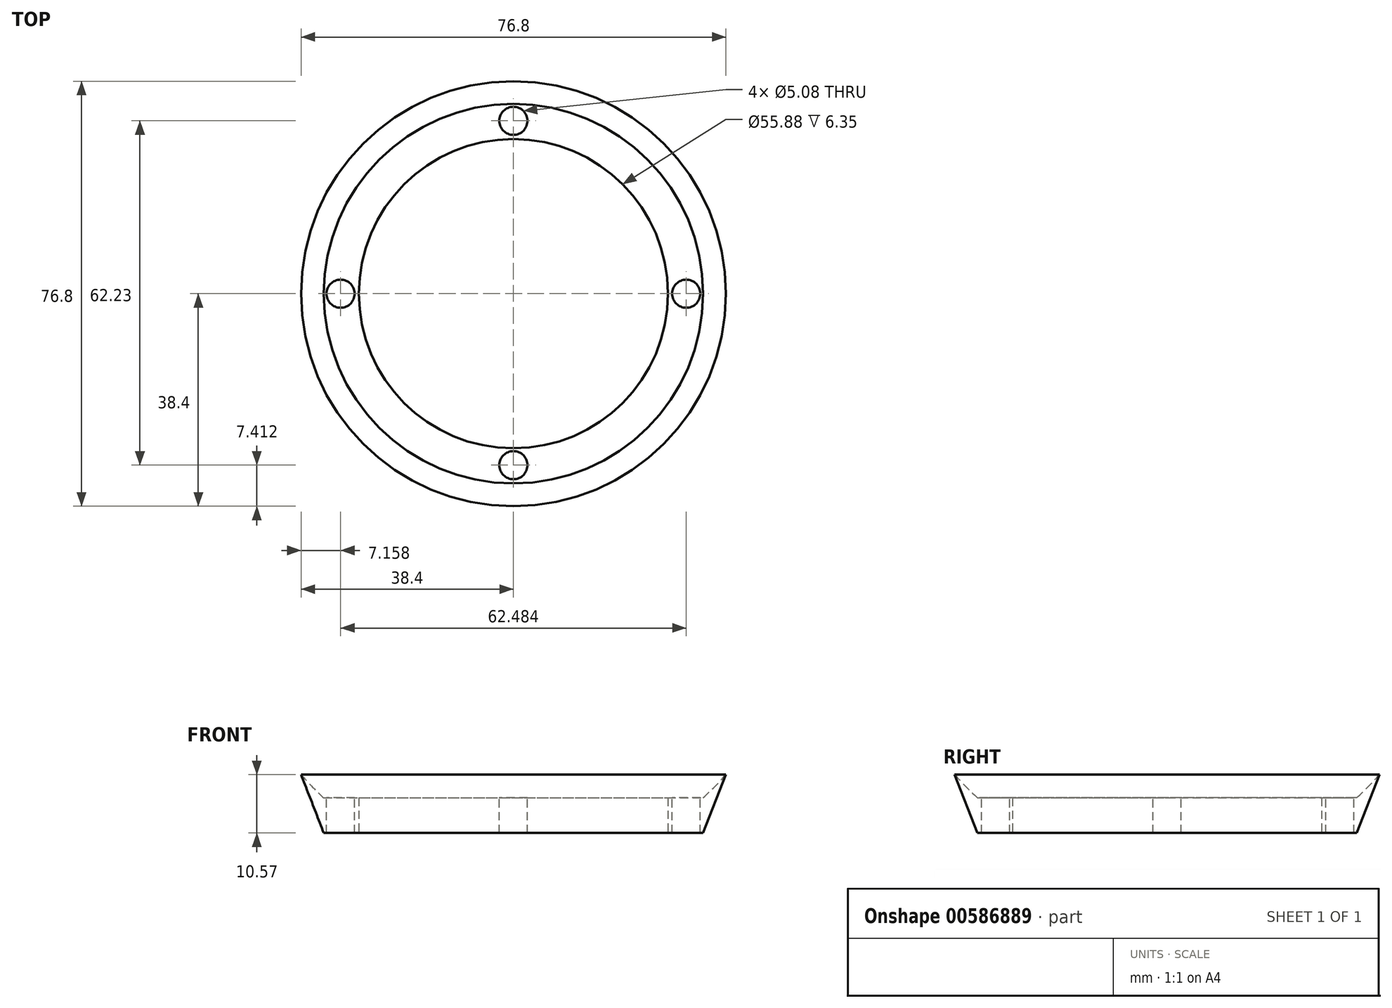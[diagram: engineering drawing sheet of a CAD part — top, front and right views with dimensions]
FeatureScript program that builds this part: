
annotation { "Feature Type Name" : "Feature", "Feature Type Description" : "" }
export const myFeature = defineFeature(function(context is Context, id is Id, definition is map)
    precondition{}
    {
        {
            var Q0;
            Q0=qCreatedBy(makeId("Front.planeOp"),FACE);
            var sketch = newSketch(context, id + "F0", { "sketchPlane" : qUnion([Q0])});
            skArc(sketch, "E0", {"start": v(0, 50.8) * mm, "mid": v(47.35, 18.4) * mm, "end": v(34.3, -37.48) * mm});
            skArc(sketch, "E1.0", {"start": v(0, 48.26) * mm, "mid": v(44.99, 17.47) * mm, "end": v(32.58, -35.6) * mm});
            skLineSegment(sketch, "E2", {"start": v(32.58, -35.6) * mm, "end": v(34.3, -37.48) * mm});
            skLineSegment(sketch, "E3", {"start": v(0, 48.26) * mm, "end": v(0, 50.8) * mm});
            skLineSegment(sketch, "E4.bottom", {"start": v(34.3, -37.48) * mm, "end": v(27.94, -37.48) * mm});
            skLineSegment(sketch, "E4.top", {"start": v(34.3, -43.83) * mm, "end": v(27.94, -43.83) * mm});
            skLineSegment(sketch, "E4.left", {"start": v(34.3, -37.48) * mm, "end": v(34.3, -43.83) * mm});
            skLineSegment(sketch, "E4.right", {"start": v(27.94, -37.48) * mm, "end": v(27.94, -43.83) * mm});
            skLineSegment(sketch, "E5", {"start": v(32.58, -35.6) * mm, "end": v(27.94, -37.48) * mm});
            skLineSegment(sketch, "E6", {"start": v(34.3, -43.83) * mm, "end": v(38.4, -33.26) * mm});
            skSolve(sketch);
        }
        {
            var Q0;
            Q0=makeQuery(id+"F0.imprint","IMPRINT",FACE,{"disambiguationData":[TD([[makeQuery(id+"F0.imprint","IMPRINT",EDGE,{"derivedFrom":sQuery(id+"F0.wireOp",EDGE,"E0")}),-1.0]])]});
            var Q1;
            Q1=makeQuery(id+"F0.imprint","IMPRINT",FACE,{"disambiguationData":[TD([[makeQuery(id+"F0.imprint","IMPRINT",EDGE,{"derivedFrom":sQuery(id+"F0.wireOp",EDGE,"E4.bottom")}),1.0]])]});
            var Q2;
            {var subQ0=sQuery(id+"F0.wireOp",EDGE,"E4.left");Q2=makeQuery(id+"F0.imprint","IMPRINT",FACE,{"disambiguationData":[TD([[makeQuery(id+"F0.imprint","IMPRINT",EDGE,{"derivedFrom":subQ0}),1.0]])]});}
            var Q3;
            Q3=sQuery(id+"F0.wireOp",EDGE,"E3");
            revolve(context, id + "F1", {"entities" : qUnion([Q0, Q1, Q2]), "axis" : qUnion([Q3]), "revolveType" : RevolveType.FULL});
        }
        {
            var Q0;
            Q0=sQuery(id+"F0.wireOp",VERTEX,"E1.0.center");
            var Q1;
            Q1=makeQuery(id+"F1.opRevolve","SWEPT_BODY",BODY,{"disambiguationData":[OSD([sQuery(id+"F0.wireOp",EDGE,"E0"),sQuery(id+"F0.wireOp",EDGE,"E1.0"),sQuery(id+"F0.wireOp",EDGE,"E2"),sQuery(id+"F0.wireOp",EDGE,"E3")])]});
            hole(context, id + "F2", {"style" : HoleStyle.SIMPLE, "endStyle" : HoleEndStyle.THROUGH, "oppositeDirection" : true, "holeDiameter" : 25.4 * mm, "majorDiameter" : 6.35 * mm, "isTappedThrough" : true, "tappedDepth" : 12.7 * mm, "tapClearance" : 3, "startFromSketch" : true, "locations" : qUnion([Q0]), "scope" : qUnion([Q1])});
        }
        {
            var Q0;
            Q0=qCreatedBy(makeId("Top.planeOp"),FACE);
            var sketch = newSketch(context, id + "F3", { "sketchPlane" : qUnion([Q0])});
            skPoint(sketch, "E7", {"position": v(0, -31.24) * mm});
            skPoint(sketch, "E8", {"position": v(31.24, 0) * mm});
            skPoint(sketch, "E9", {"position": v(0, 31.24) * mm});
            skPoint(sketch, "E10", {"position": v(-31.24, 0) * mm});
            skSolve(sketch);
        }
        {
            var Q0;
            Q0=sQuery(id+"F3.wireOp",VERTEX,"E10");
            var Q1;
            Q1=makeQuery(id+"F1.opRevolve","SWEPT_BODY",BODY,{"disambiguationData":[OSD([sQuery(id+"F0.wireOp",EDGE,"E4.bottom"),sQuery(id+"F0.wireOp",EDGE,"E4.top"),sQuery(id+"F0.wireOp",EDGE,"E4.left"),sQuery(id+"F0.wireOp",EDGE,"E4.right")])]});
            var Q2;
            Q2=makeQuery(id+"F1.opRevolve","SWEPT_BODY",BODY,{"disambiguationData":[OSD([sQuery(id+"F0.wireOp",EDGE,"E0"),sQuery(id+"F0.wireOp",EDGE,"E1.0"),sQuery(id+"F0.wireOp",EDGE,"E2"),sQuery(id+"F0.wireOp",EDGE,"E3")])]});
            hole(context, id + "F4", {"style" : HoleStyle.SIMPLE, "endStyle" : HoleEndStyle.THROUGH, "holeDiameter" : 5.08 * mm, "majorDiameter" : 6.35 * mm, "isTappedThrough" : true, "tappedDepth" : 12.7 * mm, "tapClearance" : 3, "startFromSketch" : true, "locations" : qUnion([Q0]), "scope" : qUnion([Q1, Q2])});
        }
        {
            var Q0;
            Q0=qCreatedBy(makeId("Top.planeOp"),FACE);
            var sketch = newSketch(context, id + "F5", { "sketchPlane" : qUnion([Q0])});
            skPoint(sketch, "E11", {"position": v(0, -30.99) * mm});
            skPoint(sketch, "E12", {"position": v(0, 30.99) * mm});
            skSolve(sketch);
        }
        {
            var Q0;
            Q0=sQuery(id+"F5.wireOp",VERTEX,"E11");
            var Q1;
            Q1=makeQuery(id+"F1.opRevolve","SWEPT_BODY",BODY,{"disambiguationData":[OSD([sQuery(id+"F0.wireOp",EDGE,"E4.bottom"),sQuery(id+"F0.wireOp",EDGE,"E4.top"),sQuery(id+"F0.wireOp",EDGE,"E4.left"),sQuery(id+"F0.wireOp",EDGE,"E4.right")])]});
            var Q2;
            Q2=makeQuery(id+"F1.opRevolve","SWEPT_BODY",BODY,{"disambiguationData":[OSD([sQuery(id+"F0.wireOp",EDGE,"E0"),sQuery(id+"F0.wireOp",EDGE,"E1.0"),sQuery(id+"F0.wireOp",EDGE,"E2"),sQuery(id+"F0.wireOp",EDGE,"E3")])]});
            hole(context, id + "F6", {"style" : HoleStyle.SIMPLE, "endStyle" : HoleEndStyle.THROUGH, "holeDiameter" : 5.08 * mm, "majorDiameter" : 6.35 * mm, "isTappedThrough" : true, "tappedDepth" : 12.7 * mm, "tapClearance" : 3, "startFromSketch" : true, "locations" : qUnion([Q0]), "scope" : qUnion([Q1, Q2])});
        }
        {
            var Q0;
            Q0=sQuery(id+"F3.wireOp",VERTEX,"E9");
            var Q1;
            Q1=sQuery(id+"F3.wireOp",VERTEX,"E8");
            var Q2;
            Q2=makeQuery(id+"F1.opRevolve","SWEPT_BODY",BODY,{"disambiguationData":[OSD([sQuery(id+"F0.wireOp",EDGE,"E4.bottom"),sQuery(id+"F0.wireOp",EDGE,"E4.top"),sQuery(id+"F0.wireOp",EDGE,"E4.left"),sQuery(id+"F0.wireOp",EDGE,"E4.right")])]});
            var Q3;
            Q3=makeQuery(id+"F1.opRevolve","SWEPT_BODY",BODY,{"disambiguationData":[OSD([sQuery(id+"F0.wireOp",EDGE,"E0"),sQuery(id+"F0.wireOp",EDGE,"E1.0"),sQuery(id+"F0.wireOp",EDGE,"E2"),sQuery(id+"F0.wireOp",EDGE,"E3")])]});
            hole(context, id + "F7", {"style" : HoleStyle.SIMPLE, "endStyle" : HoleEndStyle.THROUGH, "holeDiameter" : 5.08 * mm, "majorDiameter" : 6.35 * mm, "isTappedThrough" : true, "tappedDepth" : 12.7 * mm, "tapClearance" : 3, "startFromSketch" : true, "locations" : qUnion([Q0, Q1]), "scope" : qUnion([Q2, Q3])});
        }
    });
